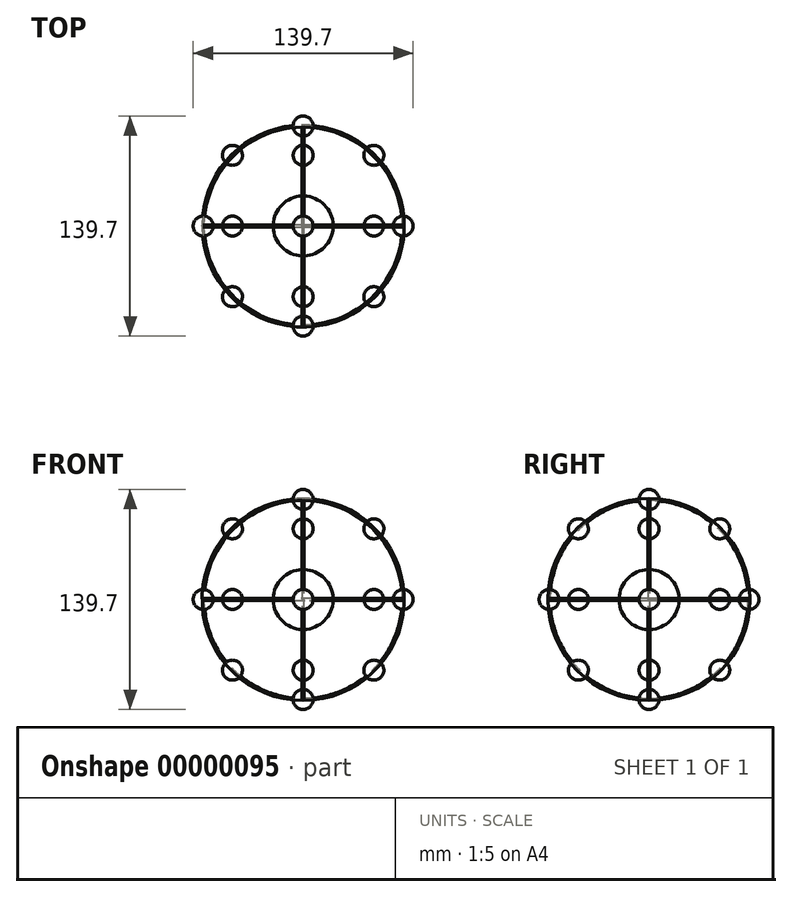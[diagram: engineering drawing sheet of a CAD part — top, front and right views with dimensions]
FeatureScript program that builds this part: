
annotation { "Feature Type Name" : "Feature", "Feature Type Description" : "" }
export const myFeature = defineFeature(function(context is Context, id is Id, definition is map)
    precondition{}
    {
        {
            var Q0;
            Q0=qCreatedBy(makeId("Front.planeOp"),FACE);
            var sketch = newSketch(context, id + "F0", { "sketchPlane" : qUnion([Q0])});
            skArc(sketch, "E0", {"start": v(-63.5, 6.35) * mm, "mid": v(-69.85, 0) * mm, "end": v(-63.5, -6.35) * mm});
            skLineSegment(sketch, "E1", {"start": v(-63.5, 6.35) * mm, "end": v(-63.5, -6.35) * mm});
            skSolve(sketch);
        }
        {
            var Q0;
            Q0=makeQuery(id+"F0.imprint","IMPRINT",FACE,{"disambiguationData":[TD([[makeQuery(id+"F0.imprint","IMPRINT",EDGE,{"derivedFrom":sQuery(id+"F0.wireOp",EDGE,"E0")}),1.0]])]});
            var Q1;
            Q1=sQuery(id+"F0.wireOp",EDGE,"E1");
            revolve(context, id + "F1", {"entities" : qUnion([Q0]), "axis" : qUnion([Q1]), "revolveType" : RevolveType.FULL});
        }
        {
            var Q0;
            Q0=qCreatedBy(makeId("Front.planeOp"),FACE);
            var sketch = newSketch(context, id + "F2", { "sketchPlane" : qUnion([Q0])});
            skLineSegment(sketch, "E2", {"start": v(0, 0) * mm, "end": v(0, 27.6) * mm, "construction": true});
            skSolve(sketch);
        }
        {
            var Q0;
            Q0=qCreatedBy(makeId("Front.planeOp"),FACE);
            var sketch = newSketch(context, id + "F3", { "sketchPlane" : qUnion([Q0])});
            skCircle(sketch, "E3", {"center": v(0, 0) * mm, "radius": 63.5 * mm, "construction": true});
            skLineSegment(sketch, "E4", {"start": v(0, 0) * mm, "end": v(-44.9, 44.9) * mm, "construction": true});
            skLineSegment(sketch, "E5", {"start": v(0, 0) * mm, "end": v(-44.9, -44.9) * mm, "construction": true});
            skLineSegment(sketch, "E6", {"start": v(0, 0) * mm, "end": v(0, -63.5) * mm, "construction": true});
            skLineSegment(sketch, "E7", {"start": v(0, 0) * mm, "end": v(0, 63.5) * mm, "construction": true});
            skLineSegment(sketch, "E8", {"start": v(0, 0) * mm, "end": v(44.9, 44.9) * mm, "construction": true});
            skLineSegment(sketch, "E9", {"start": v(0, 0) * mm, "end": v(44.9, -44.9) * mm, "construction": true});
            skLineSegment(sketch, "E10", {"start": v(0, 0) * mm, "end": v(63.5, 0) * mm, "construction": true});
            skLineSegment(sketch, "E11", {"start": v(0, 0) * mm, "end": v(-63.5, 0) * mm, "construction": true});
            skSolve(sketch);
        }
        {
            var Q0;
            Q0=qCreatedBy(makeId("Top.planeOp"),FACE);
            var sketch = newSketch(context, id + "F4", { "sketchPlane" : qUnion([Q0])});
            skLineSegment(sketch, "E12", {"start": v(0, 0) * mm, "end": v(0, -77.01) * mm, "construction": true});
            skSolve(sketch);
        }
        {
            var Q0;
            Q0=makeQuery(id+"F1.opRevolve","SWEPT_BODY",BODY,{"disambiguationData":[OSD([sQuery(id+"F0.wireOp",EDGE,"E0"),sQuery(id+"F0.wireOp",EDGE,"E1")])]});
            var Q1;
            Q1=sQuery(id+"F4.wireOp",EDGE,"E12");
            circularPattern(context, id + "F5", {"entities" : qUnion([Q0]), "axis" : qUnion([Q1]), "angle" : 180 * degree, "instanceCount" : 5, "equalSpace" : true});
        }
        {
            var Q0;
            Q0=makeQuery(id+"F5.opPattern","COPY",BODY,{"derivedFrom":makeQuery(id+"F1.opRevolve","SWEPT_BODY",BODY,{"disambiguationData":[OSD([sQuery(id+"F0.wireOp",EDGE,"E0"),sQuery(id+"F0.wireOp",EDGE,"E1")])]}),"instanceName":"1"});
            var Q1;
            Q1=makeQuery(id+"F5.opPattern","COPY",BODY,{"derivedFrom":makeQuery(id+"F1.opRevolve","SWEPT_BODY",BODY,{"disambiguationData":[OSD([sQuery(id+"F0.wireOp",EDGE,"E0"),sQuery(id+"F0.wireOp",EDGE,"E1")])]}),"instanceName":"3"});
            var Q2;
            Q2=sQuery(id+"F3.wireOp",EDGE,"E11");
            circularPattern(context, id + "F6", {"entities" : qUnion([Q0, Q1]), "axis" : qUnion([Q2]), "angle" : 360 * degree, "instanceCount" : 4, "equalSpace" : true});
        }
        {
            var Q0;
            Q0=makeQuery(id+"F5.opPattern","COPY",BODY,{"derivedFrom":makeQuery(id+"F1.opRevolve","SWEPT_BODY",BODY,{"disambiguationData":[OSD([sQuery(id+"F0.wireOp",EDGE,"E0"),sQuery(id+"F0.wireOp",EDGE,"E1")])]}),"instanceName":"2"});
            var Q1;
            Q1=sQuery(id+"F3.wireOp",EDGE,"E11");
            circularPattern(context, id + "F7", {"entities" : qUnion([Q0]), "axis" : qUnion([Q1]), "angle" : 45 * degree, "instanceCount" : 8});
        }
        {
            var Q0;
            Q0=qCreatedBy(makeId("Front.planeOp"),FACE);
            var sketch = newSketch(context, id + "F8", { "sketchPlane" : qUnion([Q0])});
            skArc(sketch, "E13", {"start": v(0, 19.05) * mm, "mid": v(-19.05, 0) * mm, "end": v(0, -19.05) * mm});
            skLineSegment(sketch, "E14", {"start": v(0, 19.05) * mm, "end": v(0, -19.05) * mm});
            skSolve(sketch);
        }
        {
            var Q0;
            Q0=makeQuery(id+"F8.imprint","IMPRINT",FACE,{"disambiguationData":[TD([[makeQuery(id+"F8.imprint","IMPRINT",EDGE,{"derivedFrom":sQuery(id+"F8.wireOp",EDGE,"E13")}),1.0]])]});
            var Q1;
            Q1=sQuery(id+"F8.wireOp",EDGE,"E14");
            revolve(context, id + "F9", {"entities" : qUnion([Q0]), "axis" : qUnion([Q1]), "revolveType" : RevolveType.FULL});
        }
        {
            var Q0;
            Q0=qCreatedBy(makeId("Top.planeOp"),FACE);
            var sketch = newSketch(context, id + "F10", { "sketchPlane" : qUnion([Q0])});
            skCircle(sketch, "E15", {"center": v(-63.5, 0) * mm, "radius": 0.64 * mm});
            skSolve(sketch);
        }
        {
            var Q0;
            Q0=makeQuery(id+"F10.imprint","IMPRINT",FACE,{"disambiguationData":[TD([[makeQuery(id+"F10.imprint","IMPRINT",EDGE,{"derivedFrom":sQuery(id+"F10.wireOp",EDGE,"E15")}),1.0]])]});
            var Q1;
            Q1=sQuery(id+"F4.wireOp",EDGE,"E12");
            revolve(context, id + "F11", {"entities" : qUnion([Q0]), "axis" : qUnion([Q1]), "revolveType" : RevolveType.FULL});
        }
        {
            var Q0;
            Q0=qCreatedBy(makeId("Front.planeOp"),FACE);
            var sketch = newSketch(context, id + "F12", { "sketchPlane" : qUnion([Q0])});
            skCircle(sketch, "E16", {"center": v(-63.5, 0) * mm, "radius": 0.64 * mm});
            skSolve(sketch);
        }
        {
            var Q0;
            Q0=makeQuery(id+"F12.imprint","IMPRINT",FACE,{"disambiguationData":[TD([[makeQuery(id+"F12.imprint","IMPRINT",EDGE,{"derivedFrom":sQuery(id+"F12.wireOp",EDGE,"E16")}),1.0]])]});
            var Q1;
            Q1=sQuery(id+"F2.wireOp",EDGE,"E2");
            revolve(context, id + "F13", {"entities" : qUnion([Q0]), "axis" : qUnion([Q1]), "revolveType" : RevolveType.FULL});
        }
        {
            var Q0;
            Q0=qCreatedBy(makeId("Top.planeOp"),FACE);
            var sketch = newSketch(context, id + "F14", { "sketchPlane" : qUnion([Q0])});
            skCircle(sketch, "E17", {"center": v(0, -63.5) * mm, "radius": 0.64 * mm});
            skSolve(sketch);
        }
        {
            var Q0;
            Q0=makeQuery(id+"F14.imprint","IMPRINT",FACE,{"disambiguationData":[TD([[makeQuery(id+"F14.imprint","IMPRINT",EDGE,{"derivedFrom":sQuery(id+"F14.wireOp",EDGE,"E17")}),1.0]])]});
            var Q1;
            Q1=sQuery(id+"F3.wireOp",EDGE,"E11");
            revolve(context, id + "F15", {"entities" : qUnion([Q0]), "axis" : qUnion([Q1]), "revolveType" : RevolveType.FULL});
        }
    });
